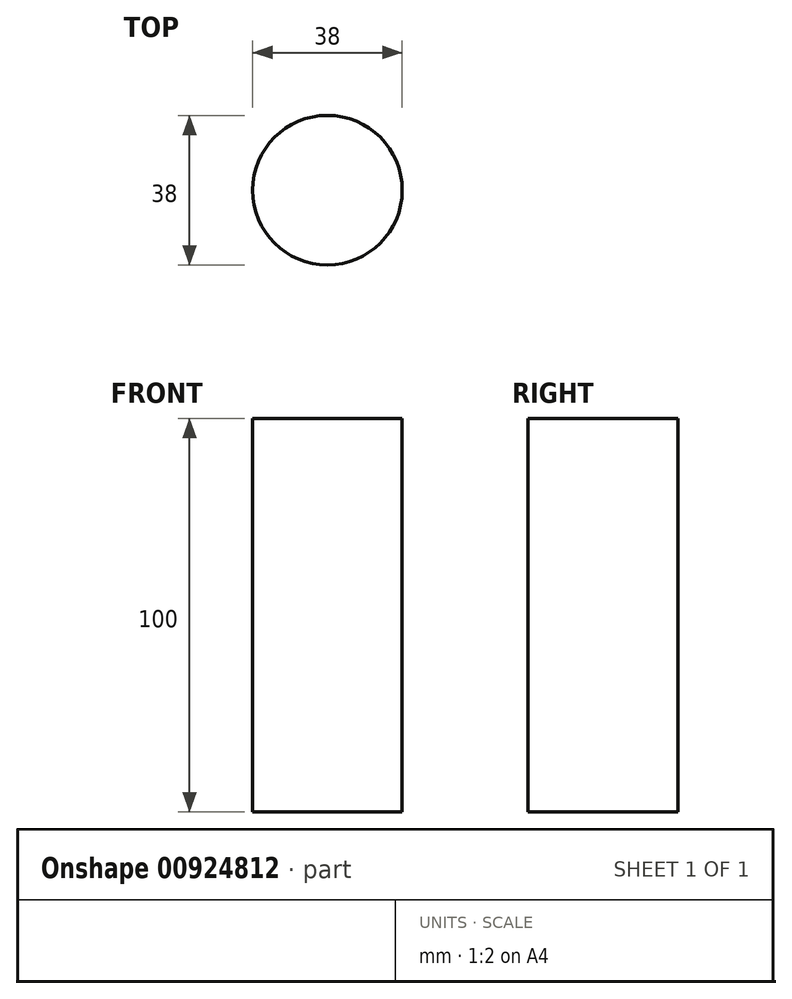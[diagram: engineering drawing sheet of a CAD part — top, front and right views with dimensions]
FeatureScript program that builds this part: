
annotation { "Feature Type Name" : "Feature", "Feature Type Description" : "" }
export const myFeature = defineFeature(function(context is Context, id is Id, definition is map)
    precondition{}
    {
        {
            var Q0;
            Q0=qCreatedBy(makeId("Top.planeOp"),FACE);
            var sketch = newSketch(context, id + "F0", { "sketchPlane" : qUnion([Q0])});
            skCircle(sketch, "E0", {"center": v(0, 0) * mm, "radius": 19 * mm});
            skSolve(sketch);
        }
        {
            var Q0;
            Q0 = qSketchRegion(id + "F0", true);
            extrude(context, id + "F1", {"entities" : qUnion([Q0]), "depth" : 100 * mm, "offsetDistance" : 25.4 * mm});
        }
    });
